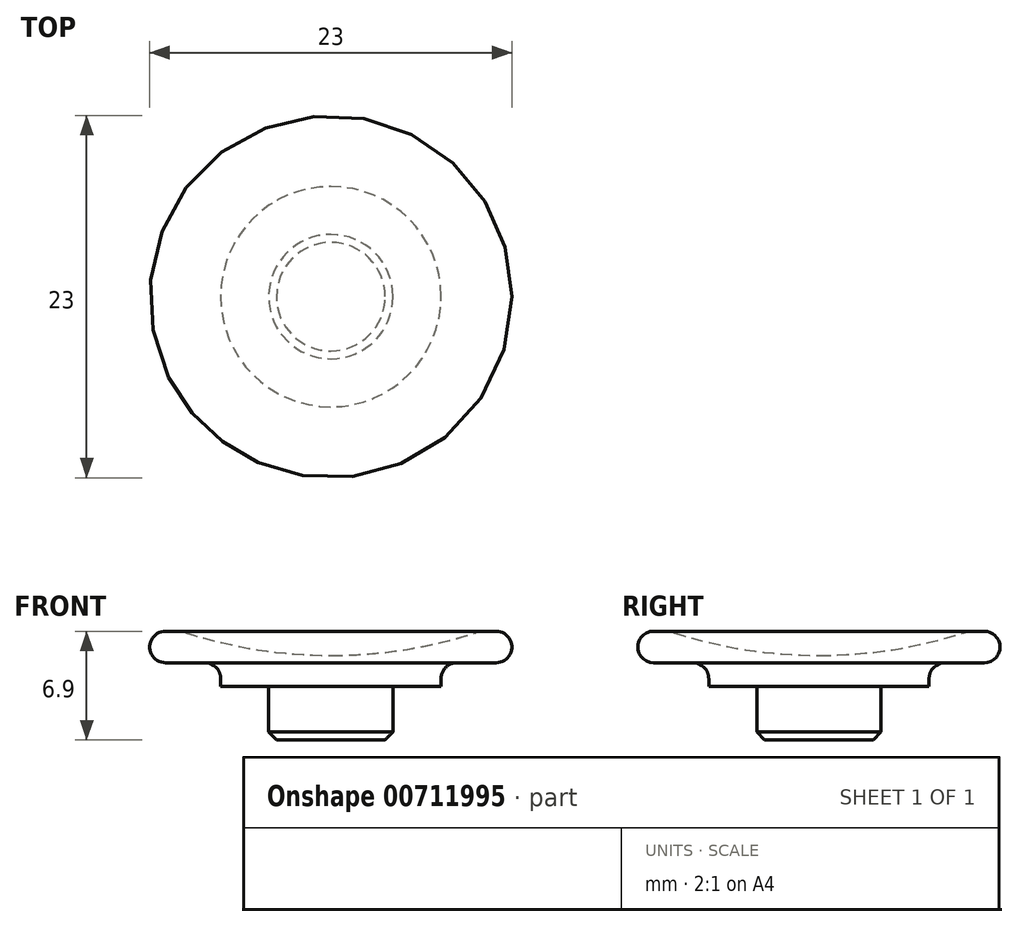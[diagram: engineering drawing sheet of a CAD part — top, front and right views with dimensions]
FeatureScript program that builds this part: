
annotation { "Feature Type Name" : "Feature", "Feature Type Description" : "" }
export const myFeature = defineFeature(function(context is Context, id is Id, definition is map)
    precondition{}
    {
        {
            var Q0;
            Q0=qCreatedBy(makeId("Front.planeOp"),FACE);
            var sketch = newSketch(context, id + "F0", { "sketchPlane" : qUnion([Q0])});
            skLineSegment(sketch, "E0.bottom", {"start": v(0, 0) * mm, "end": v(3.95, 0) * mm});
            skLineSegment(sketch, "E0.right", {"start": v(3.95, 0) * mm, "end": v(3.95, 3.4) * mm});
            skLineSegment(sketch, "E1", {"start": v(3.95, 3.4) * mm, "end": v(7, 3.4) * mm});
            skLineSegment(sketch, "E2", {"start": v(7, 3.4) * mm, "end": v(7, 3.9) * mm});
            skLineSegment(sketch, "E3", {"start": v(0, 3.4) * mm, "end": v(0, 10.15) * mm, "construction": true});
            skLineSegment(sketch, "E4", {"start": v(8, 4.9) * mm, "end": v(10.5, 4.9) * mm});
            skLineSegment(sketch, "E5", {"start": v(11.5, 5.9) * mm, "end": v(11.5, 5.9) * mm});
            skPoint(sketch, "E6.orphan", {"position": v(0, 4.9) * mm});
            skLineSegment(sketch, "E7", {"start": v(10.5, 6.9) * mm, "end": v(9.82, 6.9) * mm});
            skArc(sketch, "E8", {"start": v(0, 5.37) * mm, "mid": v(4.66, 5.73) * mm, "end": v(9.2, 6.8) * mm});
            skPoint(sketch, "E9.visualSharp", {"position": v(11.5, 4.9) * mm});
            skArc(sketch, "E9.filletArc", {"start": v(10.5, 4.9) * mm, "mid": v(11.2, 5.2) * mm, "end": v(11.5, 5.9) * mm});
            skPoint(sketch, "E10.visualSharp", {"position": v(11.5, 6.9) * mm});
            skArc(sketch, "E10.filletArc", {"start": v(11.5, 5.9) * mm, "mid": v(11.2, 6.6) * mm, "end": v(10.5, 6.9) * mm});
            skPoint(sketch, "E11.visualSharp", {"position": v(9.5, 6.9) * mm});
            skArc(sketch, "E11.filletArc", {"start": v(9.82, 6.9) * mm, "mid": v(9.5, 6.88) * mm, "end": v(9.2, 6.8) * mm});
            skPoint(sketch, "E12.visualSharp", {"position": v(7, 4.9) * mm});
            skArc(sketch, "E12.filletArc", {"start": v(8, 4.9) * mm, "mid": v(7.3, 4.6) * mm, "end": v(7, 3.9) * mm});
            skLineSegment(sketch, "E13", {"start": v(0, 5.37) * mm, "end": v(0, 0) * mm});
            skSolve(sketch);
        }
        {
            var Q0;
            Q0 = qSketchRegion(id + "F0", true);
            var Q1;
            Q1=sQuery(id+"F0.wireOp",EDGE,"E13");
            revolve(context, id + "F1", {"surfaceOperationType" : NewSurfaceOperationType.NEW, "entities" : qUnion([Q0]), "axis" : qUnion([Q1]), "revolveType" : RevolveType.FULL});
        }
        {
            var Q0;
            Q0=makeQuery(id+"F1.opRevolve","SWEPT_EDGE",EDGE,{"disambiguationData":[OSD([sQuery(id+"F0.wireOp",EDGE,"E0.bottom"),sQuery(id+"F0.wireOp",EDGE,"E0.right")])]});
            chamfer(context, id + "F2", {"entities" : qUnion([Q0]), "width" : 0.5 * mm, "tangentPropagation" : true});
        }
    });
